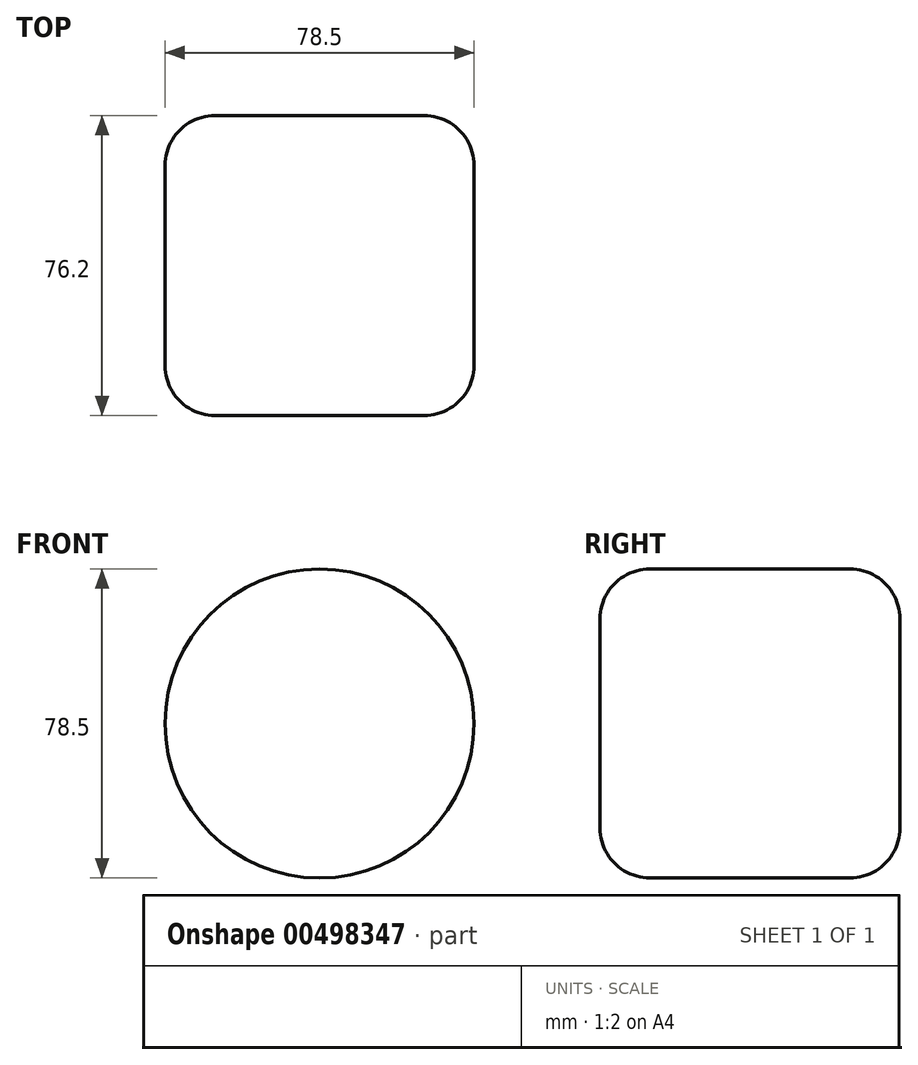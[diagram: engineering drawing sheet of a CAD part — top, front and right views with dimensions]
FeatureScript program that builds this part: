
annotation { "Feature Type Name" : "Feature", "Feature Type Description" : "" }
export const myFeature = defineFeature(function(context is Context, id is Id, definition is map)
    precondition{}
    {
        {
            var Q0;
            Q0=qCreatedBy(makeId("Front.planeOp"),FACE);
            var sketch = newSketch(context, id + "F0", { "sketchPlane" : qUnion([Q0])});
            skCircle(sketch, "E0", {"center": v(0, 0) * mm, "radius": 39.25 * mm});
            skSolve(sketch);
        }
        {
            var Q0;
            Q0=makeQuery(id+"F0.imprint","IMPRINT",FACE,{"disambiguationData":[TD([[makeQuery(id+"F0.imprint","IMPRINT",EDGE,{"derivedFrom":sQuery(id+"F0.wireOp",EDGE,"E0")}),1.0]])]});
            extrude(context, id + "F1", {"entities" : qUnion([Q0]), "depth" : 76.2 * mm});
        }
        {
            var Q0;
            Q0=makeQuery(id+"F1.opExtrude","SWEPT_FACE",FACE,{"disambiguationData":[OSD([sQuery(id+"F0.wireOp",EDGE,"E0")])]});
            fillet(context, id + "F2", {"entities" : qUnion([Q0]), "radius" : 12.7 * mm, "tangentPropagation" : true, "allowEdgeOverflow" : false});
        }
    });
